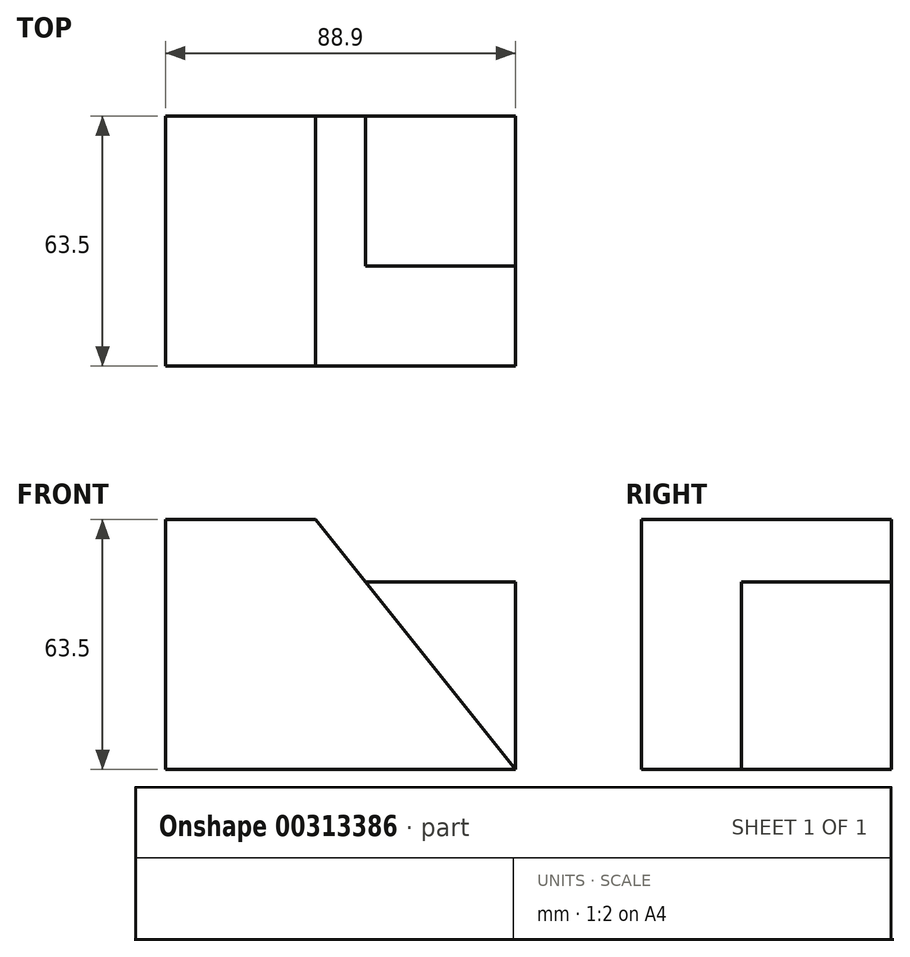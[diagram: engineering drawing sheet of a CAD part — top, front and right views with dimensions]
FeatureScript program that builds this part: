
annotation { "Feature Type Name" : "Feature", "Feature Type Description" : "" }
export const myFeature = defineFeature(function(context is Context, id is Id, definition is map)
    precondition{}
    {
        {
            var Q0;
            Q0=qCreatedBy(makeId("Front.planeOp"),FACE);
            var sketch = newSketch(context, id + "F0", { "sketchPlane" : qUnion([Q0])});
            skLineSegment(sketch, "E0", {"start": v(-47.29, 31.16) * mm, "end": v(-47.29, -32.34) * mm});
            skLineSegment(sketch, "E1", {"start": v(-47.29, -32.34) * mm, "end": v(41.61, -32.34) * mm});
            skLineSegment(sketch, "E2", {"start": v(-47.29, 31.16) * mm, "end": v(-9.19, 31.16) * mm});
            skLineSegment(sketch, "E3", {"start": v(-9.19, 31.16) * mm, "end": v(41.61, -32.34) * mm});
            skSolve(sketch);
        }
        {
            var Q0;
            Q0 = qSketchRegion(id + "F0", true);
            extrude(context, id + "F1", {"entities" : qUnion([Q0]), "depth" : 63.5 * mm});
        }
        {
            var Q0;
            Q0=makeQuery(id+"F1.opExtrude","CAP_FACE",FACE,{"disambiguationData":[OSD([sQuery(id+"F0.wireOp",EDGE,"E0"),sQuery(id+"F0.wireOp",EDGE,"E1"),sQuery(id+"F0.wireOp",EDGE,"E2"),sQuery(id+"F0.wireOp",EDGE,"E3")])],"isStart":true});
            var sketch = newSketch(context, id + "F2", { "sketchPlane" : qUnion([Q0])});
            skLineSegment(sketch, "E4", {"start": v(-41.61, -32.34) * mm, "end": v(-41.61, 15.28) * mm});
            skLineSegment(sketch, "E5", {"start": v(-41.61, 15.28) * mm, "end": v(-3.51, 15.28) * mm});
            skLineSegment(sketch, "E6", {"start": v(-3.51, 15.28) * mm, "end": v(-41.61, -32.34) * mm});
            skSolve(sketch);
        }
        {
            var Q0;
            Q0 = qSketchRegion(id + "F2", true);
            extrude(context, id + "F3", {"entities" : qUnion([Q0]), "operationType" : NewBodyOperationType.ADD, "oppositeDirection" : true, "depth" : 38.1 * mm});
        }
    });
